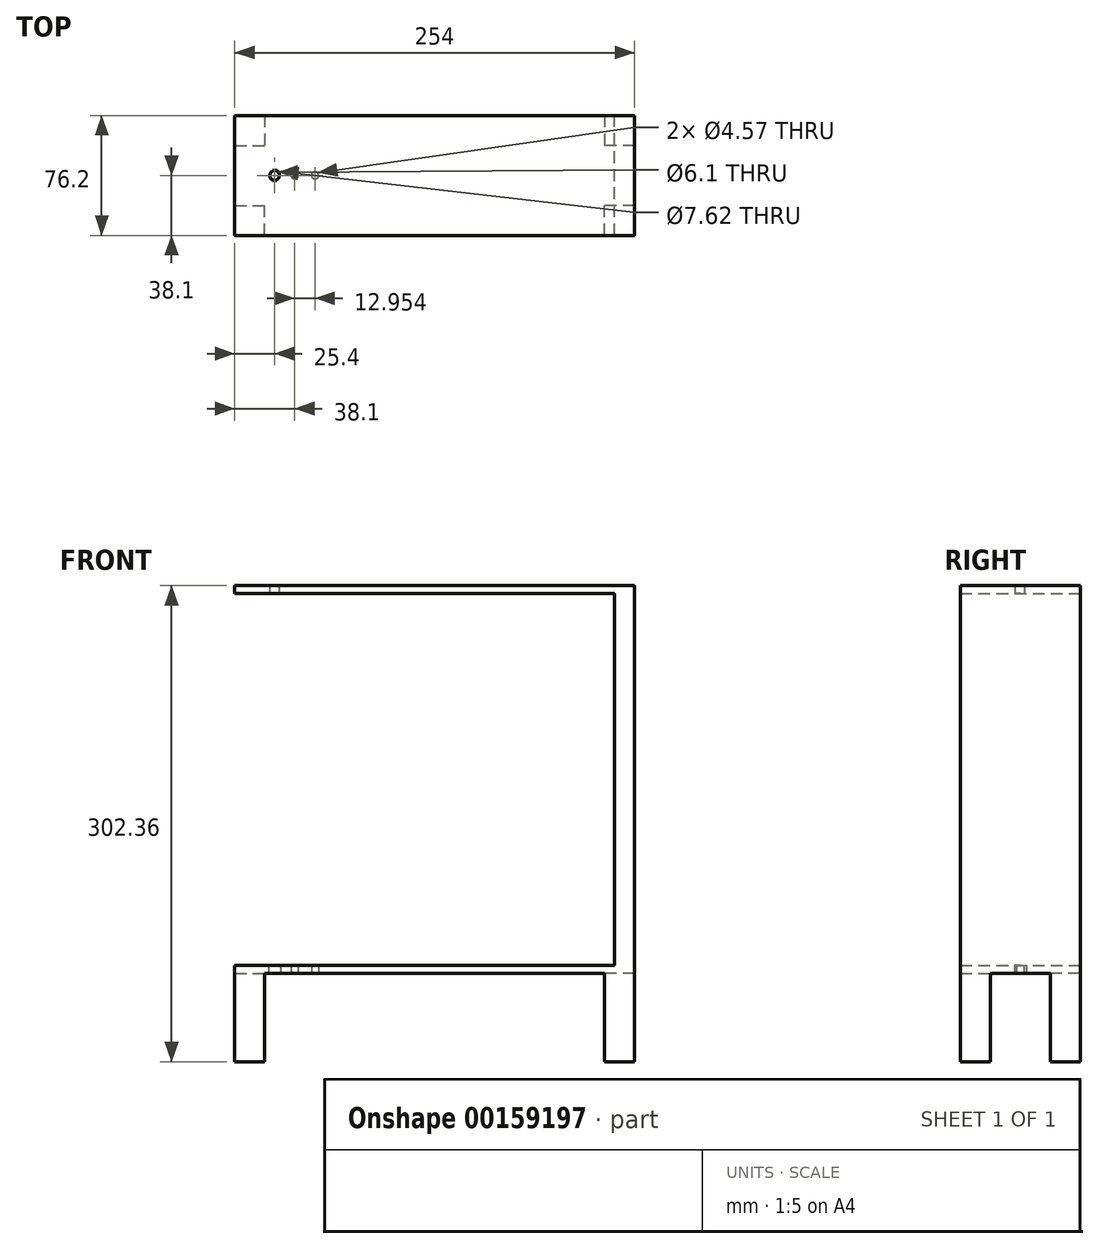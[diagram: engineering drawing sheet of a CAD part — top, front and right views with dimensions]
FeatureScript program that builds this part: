
annotation { "Feature Type Name" : "Feature", "Feature Type Description" : "" }
export const myFeature = defineFeature(function(context is Context, id is Id, definition is map)
    precondition{}
    {
        {
            var Q0;
            Q0=qCreatedBy(makeId("Front.planeOp"),FACE);
            var sketch = newSketch(context, id + "F0", { "sketchPlane" : qUnion([Q0])});
            skLineSegment(sketch, "E0.bottom", {"start": v(-127, 123.11) * mm, "end": v(127, 123.11) * mm});
            skLineSegment(sketch, "E0.top", {"start": v(-127, -123.11) * mm, "end": v(127, -123.11) * mm});
            skLineSegment(sketch, "E0.left", {"start": v(-127, 123.11) * mm, "end": v(-127, 118.03) * mm});
            skLineSegment(sketch, "E0.right", {"start": v(127, 123.11) * mm, "end": v(127, -123.11) * mm});
            skPoint(sketch, "E0.middle", {"position": v(0, 0) * mm});
            skLineSegment(sketch, "E1.bottom", {"start": v(-114.3, -118.03) * mm, "end": v(114.3, -118.03) * mm});
            skLineSegment(sketch, "E1.top", {"start": v(-114.3, 118.03) * mm, "end": v(114.3, 118.03) * mm});
            skLineSegment(sketch, "E1.right", {"start": v(114.3, -118.03) * mm, "end": v(114.3, 118.03) * mm});
            skLineSegment(sketch, "E2", {"start": v(-114.3, -118.03) * mm, "end": v(-127, -118.03) * mm});
            skLineSegment(sketch, "E3", {"start": v(-114.3, 118.03) * mm, "end": v(-127, 118.03) * mm});
            skLineSegment(sketch, "E4.trimOffspring", {"start": v(-127, -118.03) * mm, "end": v(-127, -123.11) * mm});
            skSolve(sketch);
        }
        {
            var Q0;
            Q0=makeQuery(id+"F0.imprint","IMPRINT",FACE,{"disambiguationData":[TD([[makeQuery(id+"F0.imprint","IMPRINT",EDGE,{"derivedFrom":sQuery(id+"F0.wireOp",EDGE,"E0.bottom")}),-1.0]])]});
            extrude(context, id + "F1", {"entities" : qUnion([Q0]), "endBound" : BoundingType.SYMMETRIC, "depth" : 76.2 * mm});
        }
        {
            var Q0;
            Q0=makeQuery(id+"F1.opExtrude","SWEPT_FACE",FACE,{"disambiguationData":[OSD([sQuery(id+"F0.wireOp",EDGE,"E0.bottom")])]});
            var sketch = newSketch(context, id + "F2", { "sketchPlane" : qUnion([Q0])});
            skCircle(sketch, "E5", {"center": v(-101.6, 0) * mm, "radius": 3.05 * mm});
            skSolve(sketch);
        }
        {
            var Q0;
            Q0=makeQuery(id+"F2.imprint","IMPRINT",FACE,{"disambiguationData":[TD([[makeQuery(id+"F2.imprint","IMPRINT",EDGE,{"derivedFrom":sQuery(id+"F2.wireOp",EDGE,"E5")}),1.0]])]});
            extrude(context, id + "F3", {"entities" : qUnion([Q0]), "operationType" : NewBodyOperationType.REMOVE, "endBound" : BoundingType.THROUGH_ALL, "oppositeDirection" : true, "depth" : 25.4 * mm});
        }
        {
            var Q0;
            Q0=makeQuery(id+"F1.opExtrude","SWEPT_FACE",FACE,{"disambiguationData":[OSD([sQuery(id+"F0.wireOp",EDGE,"E0.top")])]});
            var sketch = newSketch(context, id + "F4", { "sketchPlane" : qUnion([Q0])});
            skLineSegment(sketch, "E6.bottom", {"start": v(-127, 38.1) * mm, "end": v(-107.95, 38.1) * mm});
            skLineSegment(sketch, "E6.top", {"start": v(-127, 19.05) * mm, "end": v(-107.95, 19.05) * mm});
            skLineSegment(sketch, "E6.left", {"start": v(-127, 38.1) * mm, "end": v(-127, 19.05) * mm});
            skLineSegment(sketch, "E6.right", {"start": v(-107.95, 38.1) * mm, "end": v(-107.95, 19.05) * mm});
            skLineSegment(sketch, "E7.bottom", {"start": v(-127, -38.1) * mm, "end": v(-107.95, -38.1) * mm});
            skLineSegment(sketch, "E7.top", {"start": v(-127, -19.05) * mm, "end": v(-107.95, -19.05) * mm});
            skLineSegment(sketch, "E7.left", {"start": v(-127, -38.1) * mm, "end": v(-127, -19.05) * mm});
            skLineSegment(sketch, "E7.right", {"start": v(-107.95, -38.1) * mm, "end": v(-107.95, -19.05) * mm});
            skLineSegment(sketch, "E8.bottom", {"start": v(127, 38.1) * mm, "end": v(107.95, 38.1) * mm});
            skLineSegment(sketch, "E8.top", {"start": v(127, 19.05) * mm, "end": v(107.95, 19.05) * mm});
            skLineSegment(sketch, "E8.left", {"start": v(127, 38.1) * mm, "end": v(127, 19.05) * mm});
            skLineSegment(sketch, "E8.right", {"start": v(107.95, 38.1) * mm, "end": v(107.95, 19.05) * mm});
            skLineSegment(sketch, "E9.bottom", {"start": v(127, -38.1) * mm, "end": v(107.95, -38.1) * mm});
            skLineSegment(sketch, "E9.top", {"start": v(127, -19.05) * mm, "end": v(107.95, -19.05) * mm});
            skLineSegment(sketch, "E9.left", {"start": v(127, -38.1) * mm, "end": v(127, -19.05) * mm});
            skLineSegment(sketch, "E9.right", {"start": v(107.95, -38.1) * mm, "end": v(107.95, -19.05) * mm});
            skSolve(sketch);
        }
        {
            var Q0;
            Q0=makeQuery(id+"F4.imprint","IMPRINT",FACE,{"disambiguationData":[TD([[makeQuery(id+"F4.imprint","IMPRINT",EDGE,{"derivedFrom":sQuery(id+"F4.wireOp",EDGE,"E6.bottom")}),-1.0]])]});
            var Q1;
            Q1=makeQuery(id+"F4.imprint","IMPRINT",FACE,{"disambiguationData":[TD([[makeQuery(id+"F4.imprint","IMPRINT",EDGE,{"derivedFrom":sQuery(id+"F4.wireOp",EDGE,"E7.bottom")}),1.0]])]});
            var Q2;
            Q2=makeQuery(id+"F4.imprint","IMPRINT",FACE,{"disambiguationData":[TD([[makeQuery(id+"F4.imprint","IMPRINT",EDGE,{"derivedFrom":sQuery(id+"F4.wireOp",EDGE,"E8.bottom")}),-1.0]])]});
            var Q3;
            Q3=makeQuery(id+"F4.imprint","IMPRINT",FACE,{"disambiguationData":[TD([[makeQuery(id+"F4.imprint","IMPRINT",EDGE,{"derivedFrom":sQuery(id+"F4.wireOp",EDGE,"E9.bottom")}),1.0]])]});
            extrude(context, id + "F5", {"entities" : qUnion([Q0, Q1, Q2, Q3]), "operationType" : NewBodyOperationType.ADD, "depth" : 56.13 * mm});
        }
        {
            var Q0;
            Q0=makeQuery(id+"F1.opExtrude","SWEPT_FACE",FACE,{"disambiguationData":[OSD([sQuery(id+"F0.wireOp",EDGE,"E0.top")])]});
            var sketch = newSketch(context, id + "F6", { "sketchPlane" : qUnion([Q0])});
            skPoint(sketch, "E10", {"position": v(-101.6, 0) * mm});
            skCircle(sketch, "E11", {"center": v(-101.6, 0) * mm, "radius": 3.81 * mm});
            skCircle(sketch, "E12", {"center": v(-88.9, 0) * mm, "radius": 2.29 * mm});
            skCircle(sketch, "E13", {"center": v(-75.95, 0) * mm, "radius": 2.29 * mm});
            skSolve(sketch);
        }
        {
            var Q0;
            Q0=makeQuery(id+"F6.imprint","IMPRINT",FACE,{"disambiguationData":[TD([[makeQuery(id+"F6.imprint","IMPRINT",EDGE,{"derivedFrom":sQuery(id+"F6.wireOp",EDGE,"E12")}),1.0]])]});
            var Q1;
            Q1=makeQuery(id+"F6.imprint","IMPRINT",FACE,{"disambiguationData":[TD([[makeQuery(id+"F6.imprint","IMPRINT",EDGE,{"derivedFrom":sQuery(id+"F6.wireOp",EDGE,"E13")}),1.0]])]});
            var Q2;
            Q2=makeQuery(id+"F6.imprint","IMPRINT",FACE,{"disambiguationData":[TD([[makeQuery(id+"F6.imprint","IMPRINT",EDGE,{"derivedFrom":sQuery(id+"F6.wireOp",EDGE,"E11")}),1.0]])]});
            extrude(context, id + "F7", {"entities" : qUnion([Q0, Q1, Q2]), "operationType" : NewBodyOperationType.REMOVE, "oppositeDirection" : true, "depth" : 25.4 * mm});
        }
    });
